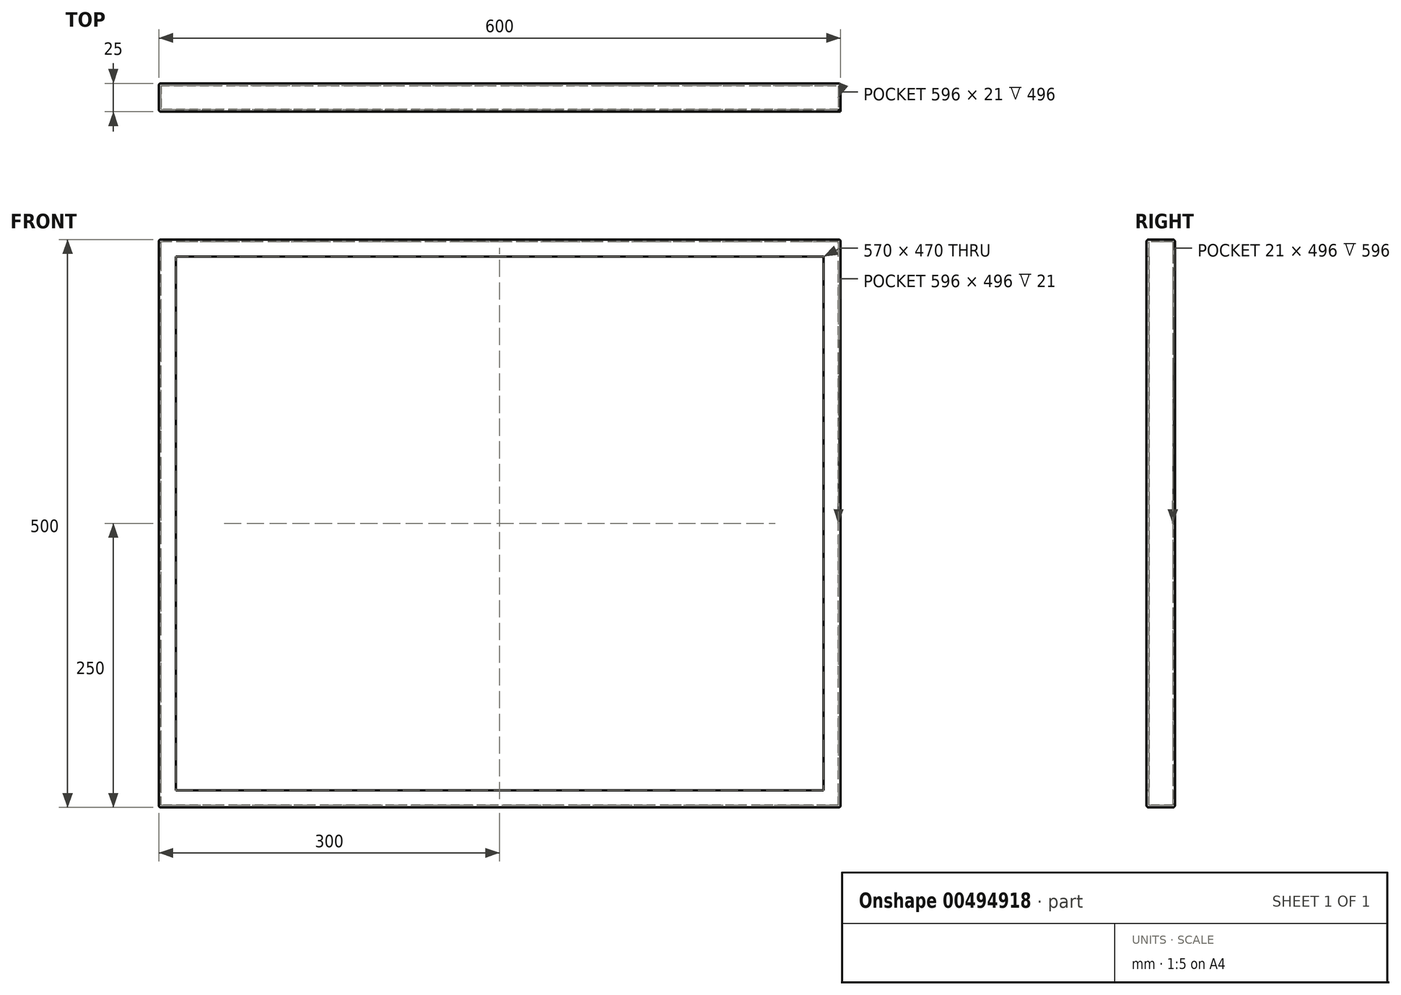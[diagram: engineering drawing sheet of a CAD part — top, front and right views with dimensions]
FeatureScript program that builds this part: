
annotation { "Feature Type Name" : "Feature", "Feature Type Description" : "" }
export const myFeature = defineFeature(function(context is Context, id is Id, definition is map)
    precondition{}
    {
        {
            var Q0;
            Q0=qCreatedBy(makeId("Front.planeOp"),FACE);
            var sketch = newSketch(context, id + "F0", { "sketchPlane" : qUnion([Q0])});
            skLineSegment(sketch, "E0.bottom", {"start": v(-300, 200) * mm, "end": v(300, 200) * mm});
            skLineSegment(sketch, "E0.top", {"start": v(-300, -300) * mm, "end": v(300, -300) * mm});
            skLineSegment(sketch, "E0.left", {"start": v(-300, 200) * mm, "end": v(-300, -300) * mm});
            skLineSegment(sketch, "E0.right", {"start": v(300, 200) * mm, "end": v(300, -300) * mm});
            skSolve(sketch);
        }
        {
            var Q0;
            Q0=qSketchRegion(id+"F0",true);
            extrude(context, id + "F1", {"entities" : qUnion([Q0]), "oppositeDirection" : true, "depth" : 25 * mm});
        }
        {
            var Q0;
            Q0=makeQuery(id+"F1.opExtrude","CAP_FACE",FACE,{"disambiguationData":[OSD([sQuery(id+"F0.wireOp",EDGE,"E0.bottom"),sQuery(id+"F0.wireOp",EDGE,"E0.top"),sQuery(id+"F0.wireOp",EDGE,"E0.left"),sQuery(id+"F0.wireOp",EDGE,"E0.right")])],"isStart":true});
            shell(context, id + "F2", {"entities" : qUnion([Q0]), "thickness" : (2) * mm});
        }
        {
            var Q0;
            Q0=qCreatedBy(makeId("Front.planeOp"),FACE);
            var sketch = newSketch(context, id + "F3", { "sketchPlane" : qUnion([Q0])});
            skLineSegment(sketch, "E1.bottom", {"start": v(-285, 185) * mm, "end": v(285, 185) * mm});
            skLineSegment(sketch, "E1.top", {"start": v(-285, -285) * mm, "end": v(285, -285) * mm});
            skLineSegment(sketch, "E1.left", {"start": v(-285, 185) * mm, "end": v(-285, -285) * mm});
            skLineSegment(sketch, "E1.right", {"start": v(285, 185) * mm, "end": v(285, -285) * mm});
            skLineSegment(sketch, "E2.bottom", {"start": v(-300, 200) * mm, "end": v(300, 200) * mm});
            skLineSegment(sketch, "E2.top", {"start": v(-300, -300) * mm, "end": v(300, -300) * mm});
            skLineSegment(sketch, "E2.left", {"start": v(-300, 200) * mm, "end": v(-300, -300) * mm});
            skLineSegment(sketch, "E2.right", {"start": v(300, 200) * mm, "end": v(300, -300) * mm});
            skSolve(sketch);
        }
        {
            var Q0;
            Q0=qSketchRegion(id+"F3",true);
            extrude(context, id + "F4", {"entities" : qUnion([Q0]), "operationType" : NewBodyOperationType.ADD, "oppositeDirection" : true, "depth" : 2 * mm});
        }
        {
            var Q0;
            Q0=makeQuery(id+"F1.opExtrude","CAP_EDGE",EDGE,{"disambiguationData":[OSD([sQuery(id+"F0.wireOp",EDGE,"E0.left")])],"isStart":false});
            var Q1;
            Q1=makeQuery(id+"F1.opExtrude","CAP_EDGE",EDGE,{"disambiguationData":[OSD([sQuery(id+"F0.wireOp",EDGE,"E0.top")])],"isStart":false});
            var Q2;
            Q2=makeQuery(id+"F1.opExtrude","CAP_EDGE",EDGE,{"disambiguationData":[OSD([sQuery(id+"F0.wireOp",EDGE,"E0.right")])],"isStart":false});
            var Q3;
            Q3=makeQuery(id+"F1.opExtrude","CAP_EDGE",EDGE,{"disambiguationData":[OSD([sQuery(id+"F0.wireOp",EDGE,"E0.bottom")])],"isStart":false});
            var Q4;
            Q4=makeQuery(id+"F1.opExtrude","CAP_EDGE",EDGE,{"disambiguationData":[OSD([sQuery(id+"F0.wireOp",EDGE,"E0.left")])],"isStart":true});
            var Q5;
            Q5=makeQuery(id+"F1.opExtrude","CAP_EDGE",EDGE,{"disambiguationData":[OSD([sQuery(id+"F0.wireOp",EDGE,"E0.bottom")])],"isStart":true});
            var Q6;
            Q6=makeQuery(id+"F1.opExtrude","CAP_EDGE",EDGE,{"disambiguationData":[OSD([sQuery(id+"F0.wireOp",EDGE,"E0.top")])],"isStart":true});
            var Q7;
            Q7=makeQuery(id+"F1.opExtrude","SWEPT_EDGE",EDGE,{"disambiguationData":[OSD([sQuery(id+"F0.wireOp",EDGE,"E0.top"),sQuery(id+"F0.wireOp",EDGE,"E0.right")])]});
            var Q8;
            Q8=makeQuery(id+"F1.opExtrude","SWEPT_EDGE",EDGE,{"disambiguationData":[OSD([sQuery(id+"F0.wireOp",EDGE,"E0.bottom"),sQuery(id+"F0.wireOp",EDGE,"E0.right")])]});
            var Q9;
            Q9=makeQuery(id+"F1.opExtrude","SWEPT_EDGE",EDGE,{"disambiguationData":[OSD([sQuery(id+"F0.wireOp",EDGE,"E0.bottom"),sQuery(id+"F0.wireOp",EDGE,"E0.left")])]});
            var Q10;
            Q10=makeQuery(id+"F1.opExtrude","SWEPT_EDGE",EDGE,{"disambiguationData":[OSD([sQuery(id+"F0.wireOp",EDGE,"E0.top"),sQuery(id+"F0.wireOp",EDGE,"E0.left")])]});
            fillet(context, id + "F5", {"entities" : qUnion([Q0, Q1, Q2, Q3, Q4, Q5, Q6, Q7, Q8, Q9, Q10]), "radius" : 2 * mm, "tangentPropagation" : true, "allowEdgeOverflow" : false});
        }
    });
